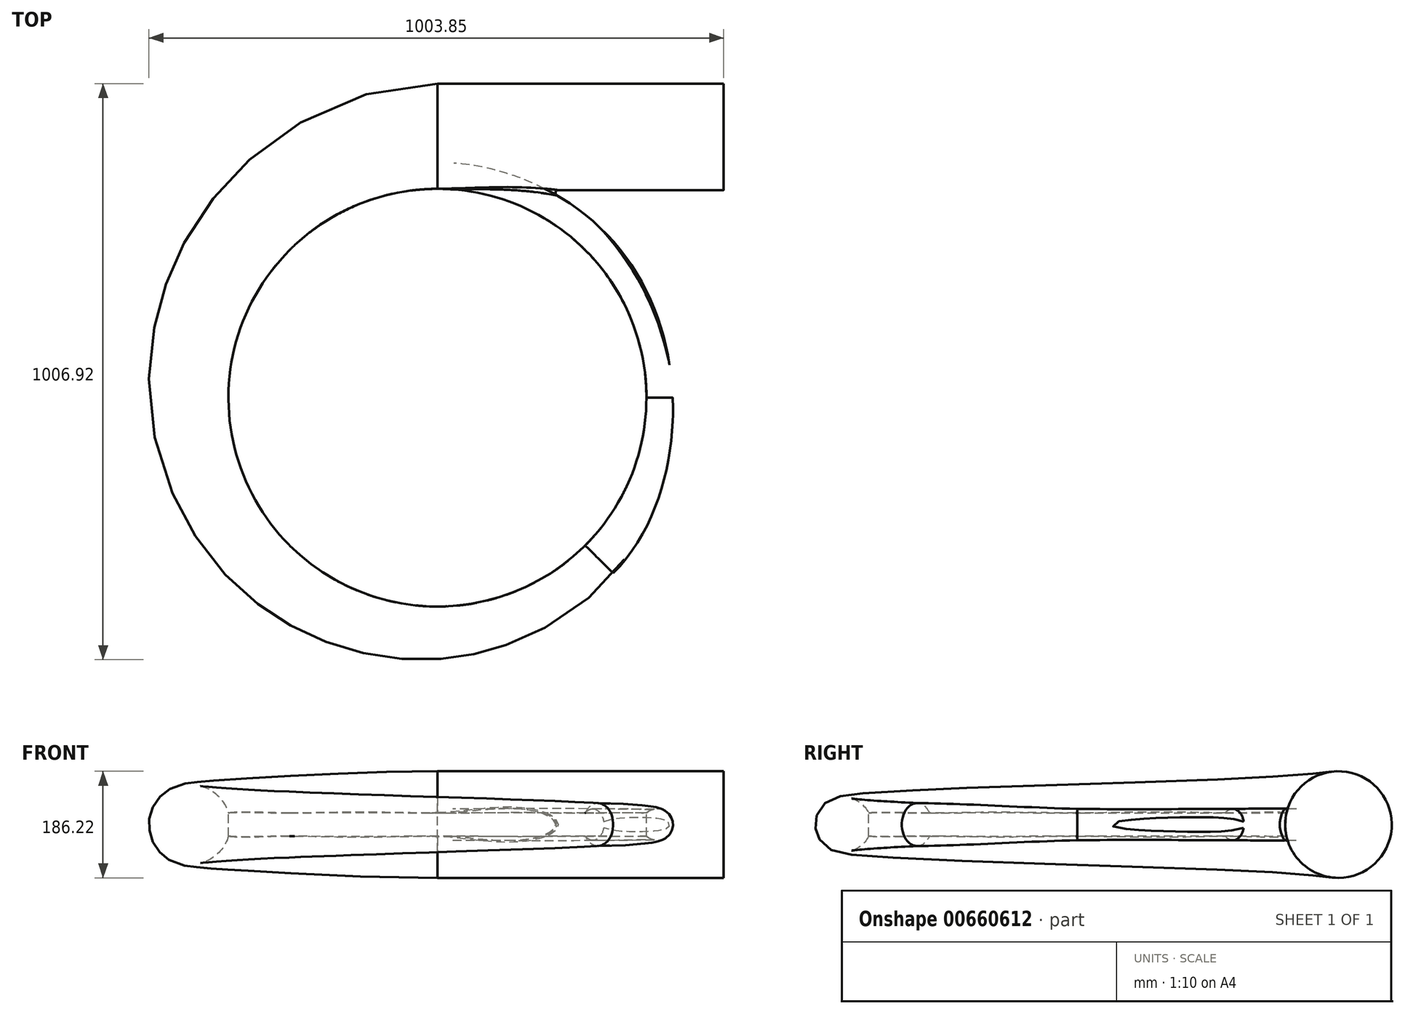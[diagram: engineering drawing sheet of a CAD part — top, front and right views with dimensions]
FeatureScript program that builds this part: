
annotation { "Feature Type Name" : "Feature", "Feature Type Description" : "" }
export const myFeature = defineFeature(function(context is Context, id is Id, definition is map)
    precondition{}
    {
        {
            var Q0;
            Q0=qCreatedBy(makeId("Top.planeOp"),FACE);
            var sketch = newSketch(context, id + "F0", { "sketchPlane" : qUnion([Q0])});
            skPoint(sketch, "E0", {"position": v(0, 365) * mm});
            skPoint(sketch, "E1", {"position": v(0, 465) * mm});
            skPoint(sketch, "E2", {"position": v(390, 0) * mm});
            skPoint(sketch, "E3", {"position": v(0, -415) * mm});
            skPoint(sketch, "E4", {"position": v(-440, 0) * mm});
            skPoint(sketch, "E5", {"position": v(-319.97, 319.97) * mm});
            skPoint(sketch, "E6", {"position": v(-302.29, -302.29) * mm});
            skPoint(sketch, "E7", {"position": v(284.61, -284.61) * mm});
            skPoint(sketch, "E8", {"position": v(266.93, 266.93) * mm});
            skPoint(sketch, "E9", {"position": v(0, 0) * mm});
            skEllipticalArc(sketch, "E10", {});
            skEllipticalArc(sketch, "E11", {});
            skEllipticalArc(sketch, "E12", {});
            skEllipticalArc(sketch, "E13", {});
            skEllipticalArc(sketch, "E14", {});
            skEllipticalArc(sketch, "E15", {});
            skEllipticalArc(sketch, "E16", {});
            skEllipticalArc(sketch, "E17", {});
            const initialGuessF0  = {"E10": [0, 0, -1, 0, 0.44, 0.46612968872584987, 5.526615742997421, 6.283185307179586], "E11": [0, 0, -0.7071067811865476, 0.7071067811865476, 0.4525, 0.4785966473523233, 5.52580766897991, 6.283185307179586], "E12": [0, 0, -1, 0, 0.44, 0.4160081858272839, 0, 0.8134183801700188], "E13": [0, 0, 0, -1, 0.415, 0.44120212867656267, 5.528380332844562, 6.283185307179586], "E14": [0, 0, 0.7071067811865496, -0.7071067811865456, 0.4025, 0.428741948548535, 5.529346229436823, 6.283185307179586], "E15": [0, 0, 1, 0, 0.39, 0.41628449735106027, 5.530375135076127, 6.283185307179586], "E16": [0, 0, 0.7071067811865476, 0.7071067811865476, 0.3775, 0.4038300656260106, 5.531473426373671, 6.283185307179586], "E17": [0, 0, 0, 1, 0.365, 0.3913789866865713, 5.532648370907622, 6.283185307179586]};
            skSetInitialGuess(sketch, initialGuessF0);
            skSolve(sketch);
        }
        {
            var Q0;
            Q0=qCreatedBy(makeId("Top.planeOp"),FACE);
            cPlane(context, id + "F1", {"entities" : qUnion([Q0]), "cplaneType" : CPlaneType.OFFSET, "offset" : 20.2 * mm, "width" : 150 * mm, "height" : 150 * mm});
        }
        {
            var Q0;
            Q0=qCreatedBy(id+"F1.planeOp",FACE);
            var sketch = newSketch(context, id + "F2", { "sketchPlane" : qUnion([Q0])});
            skPoint(sketch, "E18", {"position": v(0, 365) * mm});
            skPoint(sketch, "E19", {"position": v(0, 465) * mm});
            skPoint(sketch, "E20", {"position": v(390, 0) * mm});
            skPoint(sketch, "E21", {"position": v(0, -415) * mm});
            skPoint(sketch, "E22", {"position": v(-440, 0) * mm});
            skPoint(sketch, "E23", {"position": v(-319.97, 319.97) * mm});
            skPoint(sketch, "E24", {"position": v(-302.29, -302.29) * mm});
            skPoint(sketch, "E25", {"position": v(284.61, -284.61) * mm});
            skPoint(sketch, "E26", {"position": v(266.93, 266.93) * mm});
            skPoint(sketch, "E27", {"position": v(0, 0) * mm});
            skEllipticalArc(sketch, "E28", {});
            skEllipticalArc(sketch, "E29", {});
            skEllipticalArc(sketch, "E30", {});
            skEllipticalArc(sketch, "E31", {});
            skEllipticalArc(sketch, "E32", {});
            skEllipticalArc(sketch, "E33", {});
            skEllipticalArc(sketch, "E34", {});
            skEllipticalArc(sketch, "E35", {});
            const initialGuessF2  = {"E28": [0, 0, -1, 0, 0.44, 0.46612968872584987, 5.526615742997423, 6.283185307179586], "E29": [0, 0, -0.7071067811865476, 0.7071067811865476, 0.4525, 0.4785966473523233, 5.52580766897991, 6.283185307179586], "E30": [0, 0, -1, 0, 0.44, 0.4160081858272839, 0, 0.813418380170019], "E31": [0, 0, 0, -1, 0.415, 0.44120212867656267, 5.528380332844563, 6.283185307179586], "E32": [0, 0, 0.7071067811865496, -0.7071067811865456, 0.4025, 0.428741948548535, 5.529346229436822, 6.283185307179586], "E33": [0, 0, 1, 0, 0.39, 0.41628449735106027, 5.530375135076128, 6.283185307179586], "E34": [0, 0, 0.7071067811865476, 0.7071067811865476, 0.3775, 0.4038300656260106, 5.531473426373671, 6.283185307179586], "E35": [0, 0, 0, 1, 0.365, 0.3913789866865713, 5.532648370907622, 6.283185307179586]};
            skSetInitialGuess(sketch, initialGuessF2);
            skSolve(sketch);
        }
        {
            var Q0;
            Q0=sQuery(id+"F2.wireOp",VERTEX,"E24");
            var Q1;
            Q1=sQuery(id+"F0.wireOp",VERTEX,"E10.center");
            var Q2;
            Q2=sQuery(id+"F2.wireOp",VERTEX,"E26");
            cPlane(context, id + "F3", {"entities" : qUnion([Q0, Q1, Q2]), "cplaneType" : CPlaneType.THREE_POINT, "offset" : 25 * mm, "width" : 150 * mm, "height" : 150 * mm});
        }
        {
            var Q0;
            Q0=sQuery(id+"F2.wireOp",VERTEX,"E23");
            var Q1;
            Q1=sQuery(id+"F0.wireOp",VERTEX,"E9");
            var Q2;
            Q2=sQuery(id+"F2.wireOp",VERTEX,"E25");
            cPlane(context, id + "F4", {"entities" : qUnion([Q0, Q1, Q2]), "cplaneType" : CPlaneType.THREE_POINT, "offset" : 25 * mm, "width" : 150 * mm, "height" : 150 * mm});
        }
        {
            var Q0;
            Q0=qCreatedBy(makeId("Top.planeOp"),FACE);
            cPlane(context, id + "F5", {"entities" : qUnion([Q0]), "cplaneType" : CPlaneType.OFFSET, "offset" : 40.4 * mm, "width" : 150 * mm, "height" : 150 * mm});
        }
        {
            var Q0;
            Q0=qCreatedBy(makeId("Top.planeOp"),FACE);
            var sketch = newSketch(context, id + "F6", { "sketchPlane" : qUnion([Q0])});
            skCircle(sketch, "E36", {"center": v(0, 0) * mm, "radius": 365 * mm});
            skSolve(sketch);
        }
        {
            var Q0;
            Q0=qCreatedBy(makeId("Right.planeOp"),FACE);
            var sketch = newSketch(context, id + "F7", { "sketchPlane" : qUnion([Q0])});
            skPoint(sketch, "E37", {"position": v(365, 0) * mm});
            skPoint(sketch, "E38", {"position": v(365, 40.4) * mm});
            skPoint(sketch, "E39", {"position": v(411, 20.2) * mm});
            skArc(sketch, "E40", {"start": v(365, 0) * mm, "mid": v(411, 20.2) * mm, "end": v(365, 40.4) * mm});
            skLineSegment(sketch, "E41", {"start": v(365, 40.4) * mm, "end": v(365, 0) * mm});
            skSolve(sketch);
        }
        {
            var Q0;
            Q0=qCreatedBy(makeId("Right.planeOp"),FACE);
            var sketch = newSketch(context, id + "F8", { "sketchPlane" : qUnion([Q0])});
            skPoint(sketch, "E42", {"position": v(-365, 0) * mm});
            skPoint(sketch, "E43", {"position": v(-365, 40.4) * mm});
            skPoint(sketch, "E44", {"position": v(-457, 20.2) * mm});
            skArc(sketch, "E45", {"start": v(-365, 40.4) * mm, "mid": v(-457, 20.2) * mm, "end": v(-365, 0) * mm});
            skLineSegment(sketch, "E46", {"start": v(-365, 40.4) * mm, "end": v(-365, 0) * mm});
            skSolve(sketch);
        }
        {
            var Q0;
            Q0=qCreatedBy(makeId("Right.planeOp"),FACE);
            var sketch = newSketch(context, id + "F9", { "sketchPlane" : qUnion([Q0])});
            skPoint(sketch, "E47", {"position": v(365, 40.4) * mm});
            skPoint(sketch, "E48", {"position": v(365, 0) * mm});
            skPoint(sketch, "E49", {"position": v(549, 20.2) * mm});
            skArc(sketch, "E50", {"start": v(365, 0) * mm, "mid": v(549, 20.2) * mm, "end": v(365, 40.4) * mm});
            skLineSegment(sketch, "E51", {"start": v(365, 40.4) * mm, "end": v(365, 0) * mm});
            skSolve(sketch);
        }
        {
            var Q0;
            Q0=qCreatedBy(makeId("Front.planeOp"),FACE);
            var sketch = newSketch(context, id + "F10", { "sketchPlane" : qUnion([Q0])});
            skPoint(sketch, "E52", {"position": v(365, 0) * mm});
            skPoint(sketch, "E53", {"position": v(365, 40.4) * mm});
            skPoint(sketch, "E54", {"position": v(411, 20.2) * mm});
            skArc(sketch, "E55", {"start": v(365, 0) * mm, "mid": v(411, 20.2) * mm, "end": v(365, 40.4) * mm});
            skLineSegment(sketch, "E56", {"start": v(365, 40.4) * mm, "end": v(365, 0) * mm});
            skSolve(sketch);
        }
        {
            var Q0;
            Q0=qCreatedBy(makeId("Front.planeOp"),FACE);
            var sketch = newSketch(context, id + "F11", { "sketchPlane" : qUnion([Q0])});
            skPoint(sketch, "E57", {"position": v(-365, 40.4) * mm});
            skPoint(sketch, "E58", {"position": v(-365, 0) * mm});
            skPoint(sketch, "E59", {"position": v(-503, 20.2) * mm});
            skArc(sketch, "E60", {"start": v(-365, 40.4) * mm, "mid": v(-503, 20.2) * mm, "end": v(-365, 0) * mm});
            skLineSegment(sketch, "E61", {"start": v(-365, 40.4) * mm, "end": v(-365, 0) * mm});
            skSolve(sketch);
        }
        {
            var Q0;
            Q0=qCreatedBy(id+"F3.planeOp",FACE);
            var sketch = newSketch(context, id + "F12", { "sketchPlane" : qUnion([Q0])});
            skPoint(sketch, "E62", {"position": v(-365, 0) * mm});
            skPoint(sketch, "E63", {"position": v(-365, 40.4) * mm});
            skPoint(sketch, "E64", {"position": v(-411, 20.2) * mm});
            skArc(sketch, "E65", {"start": v(-365, 40.4) * mm, "mid": v(-411, 20.2) * mm, "end": v(-365, 0) * mm});
            skLineSegment(sketch, "E66", {"start": v(-365, 40.4) * mm, "end": v(-365, 0) * mm});
            skSolve(sketch);
        }
        {
            var Q0;
            Q0=qCreatedBy(id+"F3.planeOp",FACE);
            var sketch = newSketch(context, id + "F13", { "sketchPlane" : qUnion([Q0])});
            skPoint(sketch, "E67", {"position": v(365, 0) * mm});
            skPoint(sketch, "E68", {"position": v(365, 40.4) * mm});
            skPoint(sketch, "E69", {"position": v(480, 20.2) * mm});
            skArc(sketch, "E70", {"start": v(365, 0) * mm, "mid": v(480, 20.2) * mm, "end": v(365, 40.4) * mm});
            skLineSegment(sketch, "E71", {"start": v(365, 40.4) * mm, "end": v(365, 0) * mm});
            skSolve(sketch);
        }
        {
            var Q0;
            Q0=qCreatedBy(id+"F4.planeOp",FACE);
            var sketch = newSketch(context, id + "F14", { "sketchPlane" : qUnion([Q0])});
            skPoint(sketch, "E72", {"position": v(-365, 0) * mm});
            skPoint(sketch, "E73", {"position": v(-365, 40.4) * mm});
            skPoint(sketch, "E74", {"position": v(-434, 20.2) * mm});
            skArc(sketch, "E75", {"start": v(-365, 40.4) * mm, "mid": v(-434, 20.2) * mm, "end": v(-365, 0) * mm});
            skLineSegment(sketch, "E76", {"start": v(-365, 40.4) * mm, "end": v(-365, 0) * mm});
            skSolve(sketch);
        }
        {
            var Q0;
            Q0=qCreatedBy(id+"F4.planeOp",FACE);
            var sketch = newSketch(context, id + "F15", { "sketchPlane" : qUnion([Q0])});
            skPoint(sketch, "E77", {"position": v(365, 0) * mm});
            skPoint(sketch, "E78", {"position": v(365, 40.4) * mm});
            skPoint(sketch, "E79", {"position": v(526, 20.2) * mm});
            skArc(sketch, "E80", {"start": v(365, 0) * mm, "mid": v(526, 20.2) * mm, "end": v(365, 40.4) * mm});
            skLineSegment(sketch, "E81", {"start": v(365, 40.4) * mm, "end": v(365, 0) * mm});
            skSolve(sketch);
        }
        {
            var Q0;
            Q0=makeQuery(id+"F9.imprint","IMPRINT",FACE,{"disambiguationData":[TD([[makeQuery(id+"F9.imprint","IMPRINT",EDGE,{"derivedFrom":sQuery(id+"F9.wireOp",EDGE,"E50")}),1.0]])]});
            var Q1;
            Q1=makeQuery(id+"F15.imprint","IMPRINT",FACE,{"disambiguationData":[TD([[makeQuery(id+"F15.imprint","IMPRINT",EDGE,{"derivedFrom":sQuery(id+"F15.wireOp",EDGE,"E80")}),1.0]])]});
            var Q2;
            Q2=makeQuery(id+"F11.imprint","IMPRINT",FACE,{"disambiguationData":[TD([[makeQuery(id+"F11.imprint","IMPRINT",EDGE,{"derivedFrom":sQuery(id+"F11.wireOp",EDGE,"E60")}),1.0]])]});
            var Q3;
            Q3=makeQuery(id+"F13.imprint","IMPRINT",FACE,{"disambiguationData":[TD([[makeQuery(id+"F13.imprint","IMPRINT",EDGE,{"derivedFrom":sQuery(id+"F13.wireOp",EDGE,"E70")}),1.0]])]});
            var Q4;
            Q4=makeQuery(id+"F8.imprint","IMPRINT",FACE,{"disambiguationData":[TD([[makeQuery(id+"F8.imprint","IMPRINT",EDGE,{"derivedFrom":sQuery(id+"F8.wireOp",EDGE,"E45")}),1.0]])]});
            var Q5;
            Q5=makeQuery(id+"F14.imprint","IMPRINT",FACE,{"disambiguationData":[TD([[makeQuery(id+"F14.imprint","IMPRINT",EDGE,{"derivedFrom":sQuery(id+"F14.wireOp",EDGE,"E75")}),1.0]])]});
            var Q6;
            Q6=makeQuery(id+"F10.imprint","IMPRINT",FACE,{"disambiguationData":[TD([[makeQuery(id+"F10.imprint","IMPRINT",EDGE,{"derivedFrom":sQuery(id+"F10.wireOp",EDGE,"E55")}),1.0]])]});
            var Q7;
            Q7=makeQuery(id+"F12.imprint","IMPRINT",FACE,{"disambiguationData":[TD([[makeQuery(id+"F12.imprint","IMPRINT",EDGE,{"derivedFrom":sQuery(id+"F12.wireOp",EDGE,"E65")}),1.0]])]});
            var Q8;
            Q8=qConstructionFilter(qBodyType(qCreatedBy(id+"F9",EDGE),BodyType.WIRE),ConstructionObject.NO);
            var Q9;
            Q9=qConstructionFilter(qBodyType(qCreatedBy(id+"F15",EDGE),BodyType.WIRE),ConstructionObject.NO);
            var Q10;
            Q10=qConstructionFilter(qBodyType(qCreatedBy(id+"F11",EDGE),BodyType.WIRE),ConstructionObject.NO);
            var Q11;
            Q11=sQuery(id+"F13.wireOp",EDGE,"E70");
            var Q12;
            Q12=sQuery(id+"F8.wireOp",EDGE,"E45");
            loft(context, id + "F16", {"startCondition" : LoftEndDerivativeType.NORMAL_TO_PROFILE, "startMagnitude" : 1, "endCondition" : LoftEndDerivativeType.NORMAL_TO_PROFILE, "endMagnitude" : 1, "sheetProfilesArray" : [{ "sheetProfileEntities" : qUnion([Q0]) }, { "sheetProfileEntities" : qUnion([Q1]) }, { "sheetProfileEntities" : qUnion([Q2]) }, { "sheetProfileEntities" : qUnion([Q3]) }, { "sheetProfileEntities" : qUnion([Q4]) }, { "sheetProfileEntities" : qUnion([Q5]) }, { "sheetProfileEntities" : qUnion([Q6]) }, { "sheetProfileEntities" : qUnion([Q7]) }], "wireProfilesArray" : [{ "wireProfileEntities" : qUnion([Q8]) }, { "wireProfileEntities" : qUnion([Q9]) }, { "wireProfileEntities" : qUnion([Q10]) }, { "wireProfileEntities" : qUnion([Q11]) }, { "wireProfileEntities" : qUnion([Q12]) }]});
        }
        {
            var Q0;
            Q0=qCreatedBy(makeId("Right.planeOp"),FACE);
            var sketch = newSketch(context, id + "F17", { "sketchPlane" : qUnion([Q0])});
            skPoint(sketch, "E82", {"position": v(365, 40.4) * mm});
            skPoint(sketch, "E83", {"position": v(365, 0) * mm});
            skPoint(sketch, "E84", {"position": v(549, 19.97) * mm});
            skCircle(sketch, "E85", {"center": v(455.9, 20.2) * mm, "radius": 93.1 * mm});
            skSolve(sketch);
        }
        {
            var Q0;
            Q0=qSketchRegion(id+"F17",true);
            var Q1;
            Q1=qConstructionFilter(qBodyType(qCreatedBy(id+"F17",EDGE),BodyType.WIRE),ConstructionObject.NO);
            extrude(context, id + "F18", {"entities" : qUnion([Q0]), "operationType" : NewBodyOperationType.ADD, "surfaceEntities" : qUnion([Q1]), "depth" : 500 * mm, "offsetDistance" : 25 * mm});
        }
        {
            var Q0;
            Q0=qSketchRegion(id+"F14",true);
            var Q1;
            Q1=qSketchRegion(id+"F10",true);
            var Q2;
            Q2=qSketchRegion(id+"F12",true);
            var Q3;
            Q3=qSketchRegion(id+"F7",true);
            var Q4;
            Q4=qConstructionFilter(qBodyType(qCreatedBy(id+"F10",EDGE),BodyType.WIRE),ConstructionObject.NO);
            var Q5;
            Q5=qConstructionFilter(qBodyType(qCreatedBy(id+"F12",EDGE),BodyType.WIRE),ConstructionObject.NO);
            var Q6;
            Q6=qConstructionFilter(qBodyType(qCreatedBy(id+"F7",EDGE),BodyType.WIRE),ConstructionObject.NO);
            loft(context, id + "F19", {"operationType" : NewBodyOperationType.ADD, "startCondition" : LoftEndDerivativeType.NORMAL_TO_PROFILE, "startMagnitude" : 1, "endCondition" : LoftEndDerivativeType.NORMAL_TO_PROFILE, "endMagnitude" : 1, "sheetProfilesArray" : [{ "sheetProfileEntities" : qUnion([Q0]) }, { "sheetProfileEntities" : qUnion([Q1]) }, { "sheetProfileEntities" : qUnion([Q2]) }, { "sheetProfileEntities" : qUnion([Q3]) }], "wireProfilesArray" : [{ "wireProfileEntities" : qUnion([Q4]) }, { "wireProfileEntities" : qUnion([Q5]) }, { "wireProfileEntities" : qUnion([Q6]) }]});
        }
        {
            var Q0;
            Q0=qCreatedBy(makeId("Front.planeOp"),FACE);
            var sketch = newSketch(context, id + "F20", { "sketchPlane" : qUnion([Q0])});
            skLineSegment(sketch, "E86", {"start": v(0, 65.38) * mm, "end": v(0, -33.02) * mm});
            skSolve(sketch);
        }
        {
            var Q0;
            {var subQ0=sQuery(id+"F14.wireOp",EDGE,"E75");var subQ1=sQuery(id+"F14.wireOp",EDGE,"E76");var subQ2=sQuery(id+"F12.wireOp",EDGE,"E65");var subQ3=sQuery(id+"F12.wireOp",EDGE,"E66");var subQ4=sQuery(id+"F10.wireOp",EDGE,"E55");var subQ5=sQuery(id+"F10.wireOp",EDGE,"E56");var subQ6=sQuery(id+"F7.wireOp",EDGE,"E40");var subQ7=sQuery(id+"F7.wireOp",EDGE,"E41");Q0=makeQuery(id+"F19.boolean.opBoolean","INTERSECT",EDGE,{"derivedFrom":[makeQuery(id+"F18.opExtrude","SWEPT_FACE",FACE,{"disambiguationData":[OSD([sQuery(id+"F17.wireOp",EDGE,"E85")])]}),makeQuery(id+"F19.opLoft","SWEPT_FACE",FACE,{"disambiguationData":[OSD([subQ6,subQ7,subQ4,subQ5,subQ2,subQ3,subQ0,subQ1]),TDD([makeQuery(id+"F7.imprint","INTERSECT",VERTEX,{"disambiguationData":[OD(0.0)],"derivedFrom":[subQ6,subQ7]}),makeQuery(id+"F7.imprint","INTERSECT",VERTEX,{"disambiguationData":[OD(1.0)],"derivedFrom":[subQ6,subQ7]}),makeQuery(id+"F7.imprint","IMPRINT",EDGE,{"derivedFrom":subQ6}),makeQuery(id+"F10.imprint","INTERSECT",VERTEX,{"disambiguationData":[OD(0.0)],"derivedFrom":[subQ4,subQ5]}),makeQuery(id+"F10.imprint","INTERSECT",VERTEX,{"disambiguationData":[OD(1.0)],"derivedFrom":[subQ4,subQ5]}),makeQuery(id+"F10.imprint","IMPRINT",EDGE,{"derivedFrom":subQ4}),makeQuery(id+"F12.imprint","INTERSECT",VERTEX,{"disambiguationData":[OD(0.0)],"derivedFrom":[subQ2,subQ3]}),makeQuery(id+"F12.imprint","INTERSECT",VERTEX,{"disambiguationData":[OD(1.0)],"derivedFrom":[subQ2,subQ3]}),makeQuery(id+"F12.imprint","IMPRINT",EDGE,{"derivedFrom":subQ2}),makeQuery(id+"F14.imprint","INTERSECT",VERTEX,{"disambiguationData":[OD(0.0)],"derivedFrom":[subQ0,subQ1]}),makeQuery(id+"F14.imprint","INTERSECT",VERTEX,{"disambiguationData":[OD(1.0)],"derivedFrom":[subQ0,subQ1]}),makeQuery(id+"F14.imprint","IMPRINT",EDGE,{"derivedFrom":subQ0})])]})]});}
            fillet(context, id + "F21", {"entities" : qUnion([Q0]), "radius" : 5 * mm, "tangentPropagation" : true, "allowEdgeOverflow" : false});
        }
        {
            var Q0;
            Q0 = qSketchRegion(id + "F6", true);
            extrude(context, id + "F22", {"entities" : qUnion([Q0]), "operationType" : NewBodyOperationType.REMOVE, "endBound" : BoundingType.SYMMETRIC, "oppositeDirection" : true, "depth" : 1000 * mm, "offsetDistance" : 25 * mm});
        }
    });
